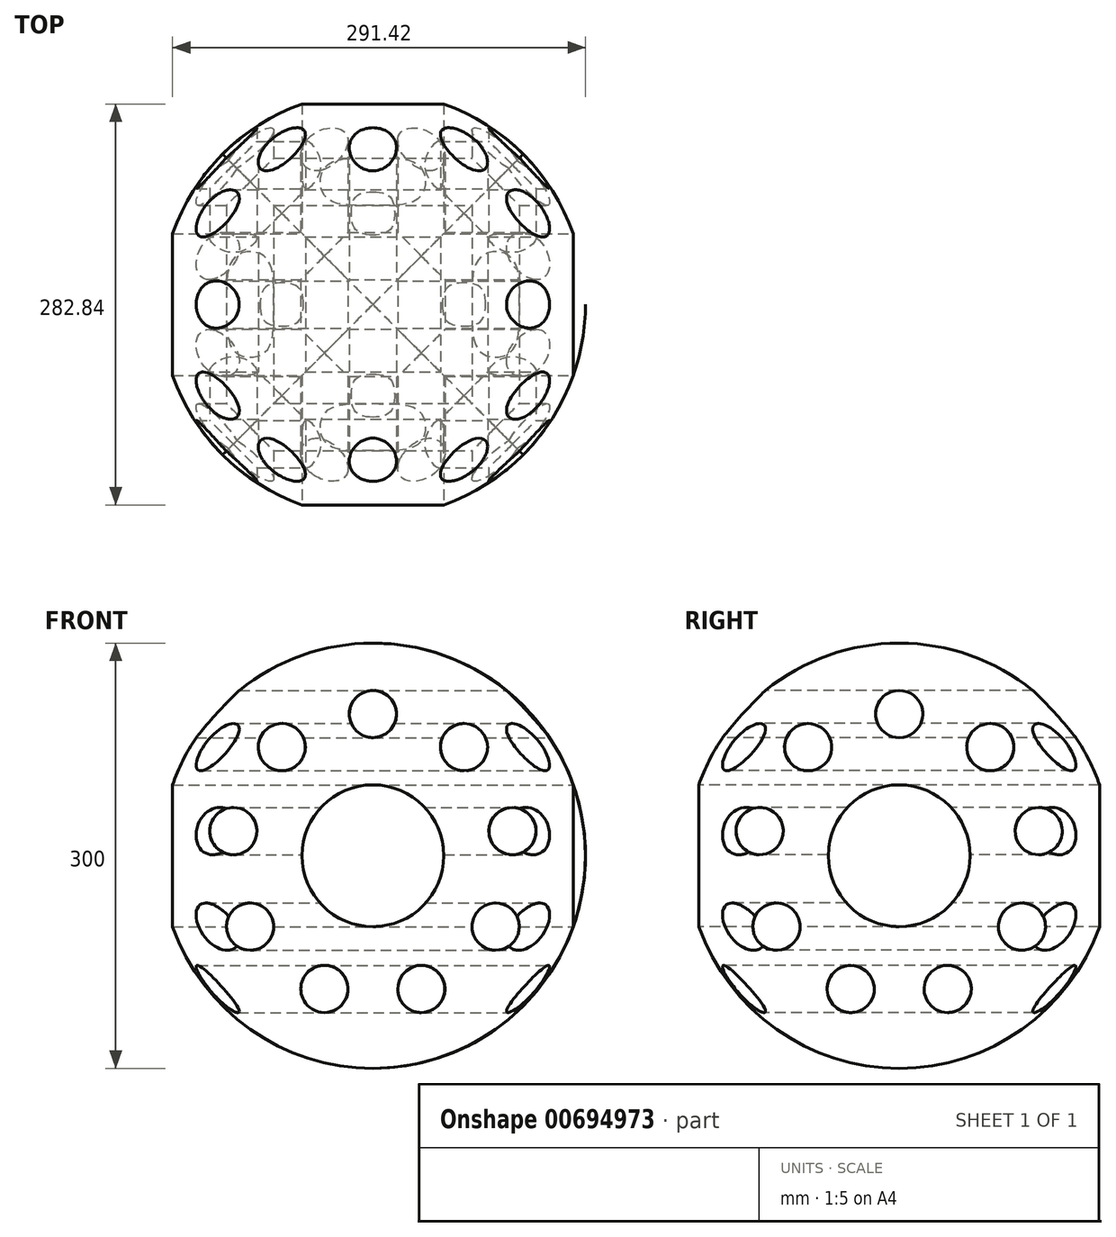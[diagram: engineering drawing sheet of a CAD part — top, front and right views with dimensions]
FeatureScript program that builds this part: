
annotation { "Feature Type Name" : "Feature", "Feature Type Description" : "" }
export const myFeature = defineFeature(function(context is Context, id is Id, definition is map)
    precondition{}
    {
        {
            var Q0;
            Q0=qCreatedBy(makeId("Front.planeOp"),FACE);
            var sketch = newSketch(context, id + "F0", { "sketchPlane" : qUnion([Q0])});
            skArc(sketch, "E0", {"start": v(0, 150) * mm, "mid": v(-150, 0) * mm, "end": v(0, -150) * mm});
            skLineSegment(sketch, "E1", {"start": v(0, 198.68) * mm, "end": v(0, -199.68) * mm, "construction": true});
            skLineSegment(sketch, "E2", {"start": v(232.5, 0) * mm, "end": v(-239.96, 0) * mm, "construction": true});
            skLineSegment(sketch, "E3", {"start": v(0, 150) * mm, "end": v(0, -150) * mm});
            skSolve(sketch);
        }
        {
            var Q0;
            Q0=makeQuery(id+"F0.imprint","IMPRINT",FACE,{"disambiguationData":[TD([[makeQuery(id+"F0.imprint","IMPRINT",EDGE,{"derivedFrom":sQuery(id+"F0.wireOp",EDGE,"E0")}),1.0]])]});
            var Q1;
            Q1=sQuery(id+"F0.wireOp",EDGE,"E1");
            revolve(context, id + "F1", {"entities" : qUnion([Q0]), "axis" : qUnion([Q1]), "revolveType" : RevolveType.FULL});
        }
        {
            var Q0;
            Q0=qCreatedBy(makeId("Front.planeOp"),FACE);
            var sketch = newSketch(context, id + "F2", { "sketchPlane" : qUnion([Q0])});
            skCircle(sketch, "E4", {"center": v(0, 0) * mm, "radius": 50 * mm});
            skCircle(sketch, "E5", {"center": v(0, 100) * mm, "radius": 16.67 * mm});
            skCircle(sketch, "E6.1.0", {"center": v(-64.28, 76.6) * mm, "radius": 16.67 * mm});
            skCircle(sketch, "E6.2.0", {"center": v(-98.48, 17.36) * mm, "radius": 16.67 * mm});
            skCircle(sketch, "E6.3.0", {"center": v(-86.6, -50) * mm, "radius": 16.67 * mm});
            skCircle(sketch, "E6.4.0", {"center": v(-34.2, -93.97) * mm, "radius": 16.67 * mm});
            skCircle(sketch, "E6.5.0", {"center": v(34.2, -93.97) * mm, "radius": 16.67 * mm});
            skCircle(sketch, "E6.6.0", {"center": v(86.6, -50) * mm, "radius": 16.67 * mm});
            skCircle(sketch, "E6.7.0", {"center": v(98.48, 17.36) * mm, "radius": 16.67 * mm});
            skCircle(sketch, "E6.8.0", {"center": v(64.28, 76.6) * mm, "radius": 16.67 * mm});
            skLineSegment(sketch, "E7", {"start": v(0, 0) * mm, "end": v(0, 191.68) * mm, "construction": true});
            skLineSegment(sketch, "E8.anchor1", {"start": v(0, 0) * mm, "end": v(0, 133.33) * mm, "construction": true});
            skLineSegment(sketch, "E8.anchor2", {"start": v(0, 0) * mm, "end": v(0, 133.33) * mm, "construction": true});
            skSolve(sketch);
        }
        {
            var Q0;
            Q0 = qSketchRegion(id + "F2", true);
            extrude(context, id + "F3", {"entities" : qUnion([Q0]), "operationType" : NewBodyOperationType.REMOVE, "endBound" : BoundingType.SYMMETRIC, "oppositeDirection" : true, "depth" : 300 * mm, "offsetDistance" : 25 * mm});
        }
        {
            var Q0;
            Q0=qCreatedBy(makeId("Right.planeOp"),FACE);
            var sketch = newSketch(context, id + "F4", { "sketchPlane" : qUnion([Q0])});
            skCircle(sketch, "E9", {"center": v(0, 0) * mm, "radius": 50 * mm});
            skCircle(sketch, "E10", {"center": v(0, 100) * mm, "radius": 16.67 * mm});
            skCircle(sketch, "E11.1.0", {"center": v(-64.28, 76.6) * mm, "radius": 16.67 * mm});
            skCircle(sketch, "E11.2.0", {"center": v(-98.48, 17.36) * mm, "radius": 16.67 * mm});
            skCircle(sketch, "E11.3.0", {"center": v(-86.6, -50) * mm, "radius": 16.67 * mm});
            skCircle(sketch, "E11.4.0", {"center": v(-34.2, -93.97) * mm, "radius": 16.67 * mm});
            skCircle(sketch, "E11.5.0", {"center": v(34.2, -93.97) * mm, "radius": 16.67 * mm});
            skCircle(sketch, "E11.6.0", {"center": v(86.6, -50) * mm, "radius": 16.67 * mm});
            skCircle(sketch, "E11.7.0", {"center": v(98.48, 17.36) * mm, "radius": 16.67 * mm});
            skCircle(sketch, "E11.8.0", {"center": v(64.28, 76.6) * mm, "radius": 16.67 * mm});
            skLineSegment(sketch, "E12", {"start": v(0, 0) * mm, "end": v(0, 191.68) * mm, "construction": true});
            skLineSegment(sketch, "E13.anchor1", {"start": v(0, 0) * mm, "end": v(0, 133.33) * mm, "construction": true});
            skLineSegment(sketch, "E13.anchor2", {"start": v(0, 0) * mm, "end": v(0, 133.33) * mm, "construction": true});
            skSolve(sketch);
        }
        {
            var Q0;
            Q0 = qSketchRegion(id + "F4", true);
            extrude(context, id + "F5", {"entities" : qUnion([Q0]), "operationType" : NewBodyOperationType.REMOVE, "endBound" : BoundingType.SYMMETRIC, "oppositeDirection" : true, "depth" : 300 * mm, "offsetDistance" : 25 * mm});
        }
    });
